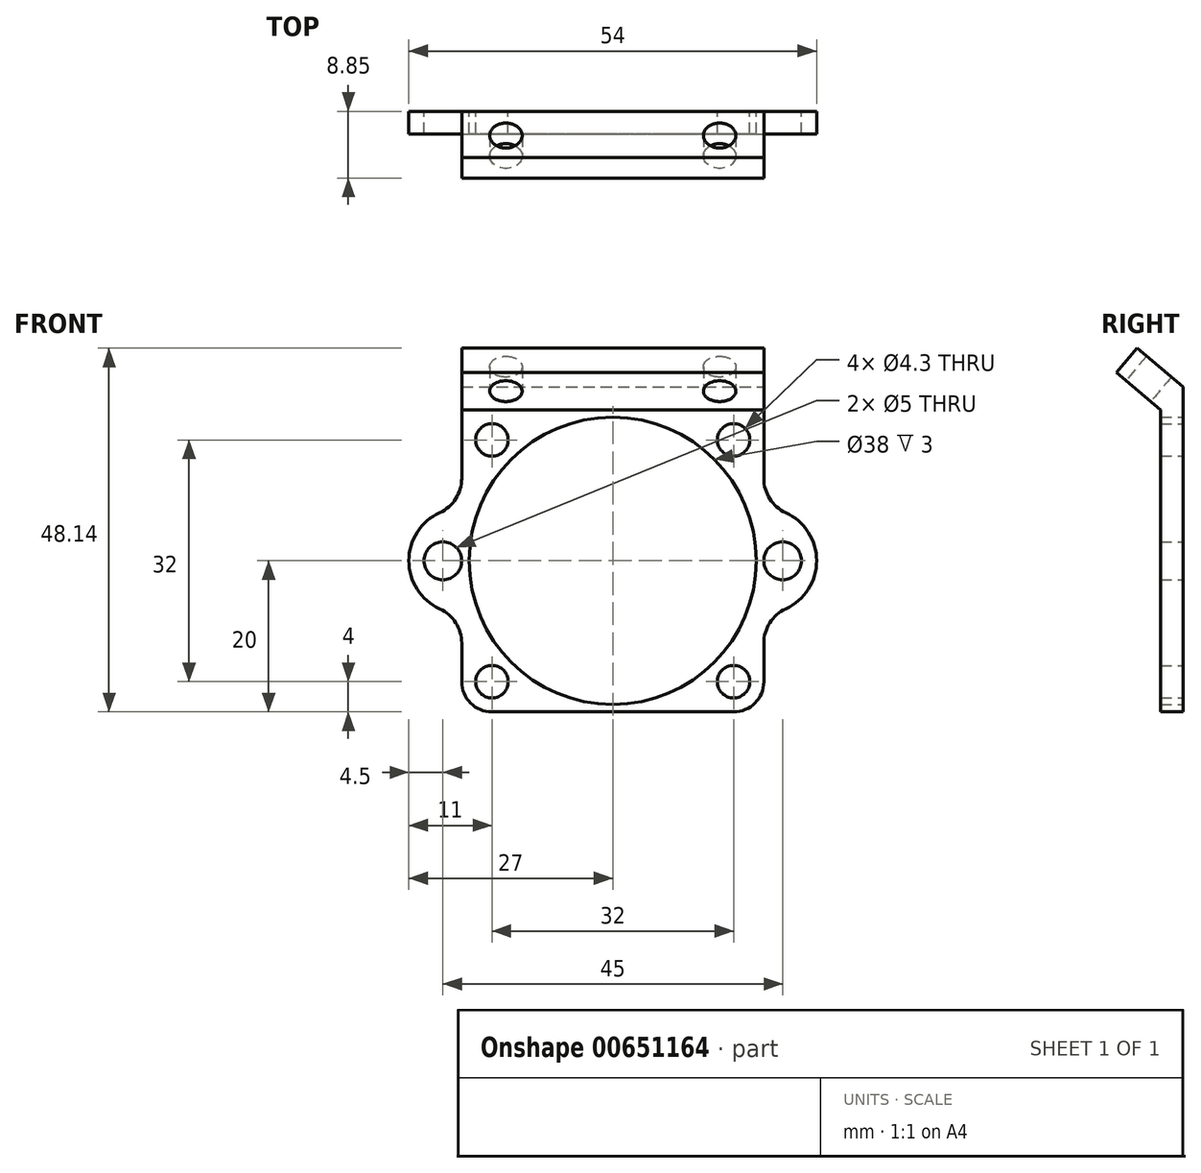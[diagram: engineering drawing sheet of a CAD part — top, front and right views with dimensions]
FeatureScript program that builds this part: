
annotation { "Feature Type Name" : "Feature", "Feature Type Description" : "" }
export const myFeature = defineFeature(function(context is Context, id is Id, definition is map)
    precondition{}
    {
        {
            var Q0;
            Q0=qCreatedBy(makeId("Front.planeOp"),FACE);
            var sketch = newSketch(context, id + "F0", { "sketchPlane" : qUnion([Q0])});
            skLineSegment(sketch, "E0.bottom", {"start": v(16, 16) * mm, "end": v(-16, 16) * mm, "construction": true});
            skLineSegment(sketch, "E0.top", {"start": v(16, -16) * mm, "end": v(-16, -16) * mm, "construction": true});
            skLineSegment(sketch, "E0.left", {"start": v(16, 16) * mm, "end": v(16, -16) * mm, "construction": true});
            skLineSegment(sketch, "E0.right", {"start": v(-16, 16) * mm, "end": v(-16, -16) * mm, "construction": true});
            skPoint(sketch, "E0.middle", {"position": v(0, 0) * mm});
            skCircle(sketch, "E1", {"center": v(-16, 16) * mm, "radius": 2.15 * mm});
            skCircle(sketch, "E2", {"center": v(16, 16) * mm, "radius": 2.15 * mm});
            skCircle(sketch, "E3", {"center": v(16, -16) * mm, "radius": 2.15 * mm});
            skCircle(sketch, "E4", {"center": v(-16, -16) * mm, "radius": 2.15 * mm});
            skLineSegment(sketch, "E5.bottom", {"start": v(20, 20) * mm, "end": v(-20, 20) * mm, "construction": true});
            skLineSegment(sketch, "E5.top", {"start": v(20, -20) * mm, "end": v(-20, -20) * mm});
            skLineSegment(sketch, "E5.left", {"start": v(20, 20) * mm, "end": v(20, -20) * mm});
            skLineSegment(sketch, "E5.right", {"start": v(-20, 20) * mm, "end": v(-20, -20) * mm});
            skCircle(sketch, "E6", {"center": v(0, 0) * mm, "radius": 19 * mm});
            skCircle(sketch, "E7", {"center": v(-22.5, 0) * mm, "radius": 2.5 * mm});
            skCircle(sketch, "E8", {"center": v(22.5, 0) * mm, "radius": 2.5 * mm});
            skArc(sketch, "E9", {"start": v(-20, 7) * mm, "mid": v(-27, 0) * mm, "end": v(-20, -7) * mm});
            skArc(sketch, "E10", {"start": v(20, 7) * mm, "mid": v(27, 0) * mm, "end": v(20, -7) * mm});
            skLineSegment(sketch, "E11.bottom", {"start": v(-20, 20) * mm, "end": v(20, 20) * mm});
            skLineSegment(sketch, "E11.top", {"start": v(-20, 23) * mm, "end": v(20, 23) * mm});
            skLineSegment(sketch, "E11.left", {"start": v(-20, 20) * mm, "end": v(-20, 23) * mm});
            skLineSegment(sketch, "E11.right", {"start": v(20, 20) * mm, "end": v(20, 23) * mm});
            skSolve(sketch);
        }
        {
            var Q0;
            Q0=makeQuery(id+"F0.imprint","IMPRINT",FACE,{"disambiguationData":[TD([[makeQuery(id+"F0.imprint","IMPRINT",EDGE,{"derivedFrom":sQuery(id+"F0.wireOp",EDGE,"E11.bottom")}),1.0]])]});
            var Q1;
            Q1=makeQuery(id+"F0.imprint","IMPRINT",FACE,{"disambiguationData":[TD([[makeQuery(id+"F0.imprint","IMPRINT",EDGE,{"derivedFrom":sQuery(id+"F0.wireOp",EDGE,"E1")}),-1.0]])]});
            var Q2;
            {var subQ2=sQuery(id+"F0.wireOp",EDGE,"E8");Q2=makeQuery(id+"F0.imprint","IMPRINT",FACE,{"disambiguationData":[TD([[makeQuery(id+"F0.imprint","IMPRINT",EDGE,{"derivedFrom":subQ2}),-1.0]])]});}
            var Q3;
            {var subQ2=sQuery(id+"F0.wireOp",EDGE,"E7");Q3=makeQuery(id+"F0.imprint","IMPRINT",FACE,{"disambiguationData":[TD([[makeQuery(id+"F0.imprint","IMPRINT",EDGE,{"derivedFrom":subQ2}),-1.0]])]});}
            extrude(context, id + "F1", {"entities" : qUnion([Q0, Q1, Q2, Q3]), "depth" : 3 * mm, "offsetDistance" : 25 * mm});
        }
        {
            var Q0;
            {var subQ0=sQuery(id+"F0.wireOp",EDGE,"E10");var subQ1=sQuery(id+"F0.wireOp",EDGE,"E5.left");Q0=makeQuery(id+"F1.opExtrude","SWEPT_EDGE",EDGE,{"disambiguationData":[OSD([subQ1,subQ0]),TDD([makeQuery(id+"F0.imprint","INTERSECT",VERTEX,{"disambiguationData":[OD(0.0)],"derivedFrom":[subQ1,subQ0]})])]});}
            var Q1;
            {var subQ0=sQuery(id+"F0.wireOp",EDGE,"E10");var subQ1=sQuery(id+"F0.wireOp",EDGE,"E5.left");Q1=makeQuery(id+"F1.opExtrude","SWEPT_EDGE",EDGE,{"disambiguationData":[OSD([subQ1,subQ0]),TDD([makeQuery(id+"F0.imprint","INTERSECT",VERTEX,{"disambiguationData":[OD(1.0)],"derivedFrom":[subQ1,subQ0]})])]});}
            var Q2;
            {var subQ0=sQuery(id+"F0.wireOp",EDGE,"E9");var subQ1=sQuery(id+"F0.wireOp",EDGE,"E5.right");Q2=makeQuery(id+"F1.opExtrude","SWEPT_EDGE",EDGE,{"disambiguationData":[OSD([subQ1,subQ0]),TDD([makeQuery(id+"F0.imprint","INTERSECT",VERTEX,{"disambiguationData":[OD(0.0)],"derivedFrom":[subQ1,subQ0]})])]});}
            var Q3;
            {var subQ0=sQuery(id+"F0.wireOp",EDGE,"E9");var subQ1=sQuery(id+"F0.wireOp",EDGE,"E5.right");Q3=makeQuery(id+"F1.opExtrude","SWEPT_EDGE",EDGE,{"disambiguationData":[OSD([subQ1,subQ0]),TDD([makeQuery(id+"F0.imprint","INTERSECT",VERTEX,{"disambiguationData":[OD(1.0)],"derivedFrom":[subQ1,subQ0]})])]});}
            fillet(context, id + "F2", {"entities" : qUnion([Q0, Q1, Q2, Q3]), "radius" : 5 * mm, "tangentPropagation" : true, "allowEdgeOverflow" : false});
        }
        {
            var Q0;
            Q0=makeQuery(id+"F1.opExtrude","SWEPT_FACE",FACE,{"disambiguationData":[OSD([sQuery(id+"F0.wireOp",EDGE,"E5.left"),sQuery(id+"F0.wireOp",EDGE,"E11.right")])]});
            var sketch = newSketch(context, id + "F3", { "sketchPlane" : qUnion([Q0])});
            skLineSegment(sketch, "E12", {"start": v(0, 23) * mm, "end": v(-6.13, 28.14) * mm});
            skLineSegment(sketch, "E13", {"start": v(-6.13, 28.14) * mm, "end": v(-8.85, 24.9) * mm});
            skLineSegment(sketch, "E14", {"start": v(-8.85, 24.9) * mm, "end": v(-3, 20) * mm});
            skSolve(sketch);
        }
        {
            var Q0;
            Q0=makeQuery(id+"F3.imprint","IMPRINT",FACE,{"disambiguationData":[TD([[makeQuery(id+"F3.imprint","IMPRINT",EDGE,{"derivedFrom":sQuery(id+"F3.wireOp",EDGE,"E12")}),1.0]])]});
            var Q1;
            Q1=makeQuery(id+"F1.opExtrude","SWEPT_FACE",FACE,{"disambiguationData":[OSD([sQuery(id+"F0.wireOp",EDGE,"E5.right"),sQuery(id+"F0.wireOp",EDGE,"E11.left")])]});
            extrude(context, id + "F4", {"entities" : qUnion([Q0]), "operationType" : NewBodyOperationType.ADD, "endBound" : BoundingType.UP_TO_SURFACE, "oppositeDirection" : true, "depth" : 25 * mm, "endBoundEntityFace" : qUnion([Q1]), "offsetDistance" : 25 * mm});
        }
        {
            var Q0;
            Q0=makeQuery(id+"F4.opExtrude","SWEPT_FACE",FACE,{"disambiguationData":[OSD([sQuery(id+"F3.wireOp",EDGE,"E14")])]});
            var sketch = newSketch(context, id + "F5", { "sketchPlane" : qUnion([Q0])});
            skLineSegment(sketch, "E15.bottom", {"start": v(-20, 22.78) * mm, "end": v(-14.15, 22.78) * mm, "construction": true});
            skLineSegment(sketch, "E15.top", {"start": v(-20, 15.15) * mm, "end": v(-14.15, 15.15) * mm, "construction": true});
            skLineSegment(sketch, "E15.left", {"start": v(-20, 22.78) * mm, "end": v(-20, 15.15) * mm, "construction": true});
            skLineSegment(sketch, "E15.right", {"start": v(-14.15, 22.78) * mm, "end": v(-14.15, 15.15) * mm, "construction": true});
            skLineSegment(sketch, "E16.bottom", {"start": v(20, 22.78) * mm, "end": v(14.15, 22.78) * mm, "construction": true});
            skLineSegment(sketch, "E16.top", {"start": v(20, 15.15) * mm, "end": v(14.15, 15.15) * mm, "construction": true});
            skLineSegment(sketch, "E16.left", {"start": v(20, 22.78) * mm, "end": v(20, 15.15) * mm, "construction": true});
            skLineSegment(sketch, "E16.right", {"start": v(14.15, 22.78) * mm, "end": v(14.15, 15.15) * mm, "construction": true});
            skCircle(sketch, "E17", {"center": v(-14.15, 18.97) * mm, "radius": 2.15 * mm});
            skCircle(sketch, "E18", {"center": v(14.15, 18.97) * mm, "radius": 2.15 * mm});
            skSolve(sketch);
        }
        {
            var Q0;
            Q0 = qSketchRegion(id + "F5", true);
            extrude(context, id + "F6", {"entities" : qUnion([Q0]), "operationType" : NewBodyOperationType.REMOVE, "oppositeDirection" : true, "depth" : 25 * mm, "offsetDistance" : 25 * mm});
        }
        {
            var Q0;
            Q0=makeQuery(id+"F1.opExtrude","SWEPT_EDGE",EDGE,{"disambiguationData":[OSD([sQuery(id+"F0.wireOp",EDGE,"E5.top"),sQuery(id+"F0.wireOp",EDGE,"E5.right")])]});
            var Q1;
            Q1=makeQuery(id+"F1.opExtrude","SWEPT_EDGE",EDGE,{"disambiguationData":[OSD([sQuery(id+"F0.wireOp",EDGE,"E5.top"),sQuery(id+"F0.wireOp",EDGE,"E5.left")])]});
            fillet(context, id + "F7", {"entities" : qUnion([Q0, Q1]), "radius" : 4 * mm, "tangentPropagation" : true, "allowEdgeOverflow" : false});
        }
    });
